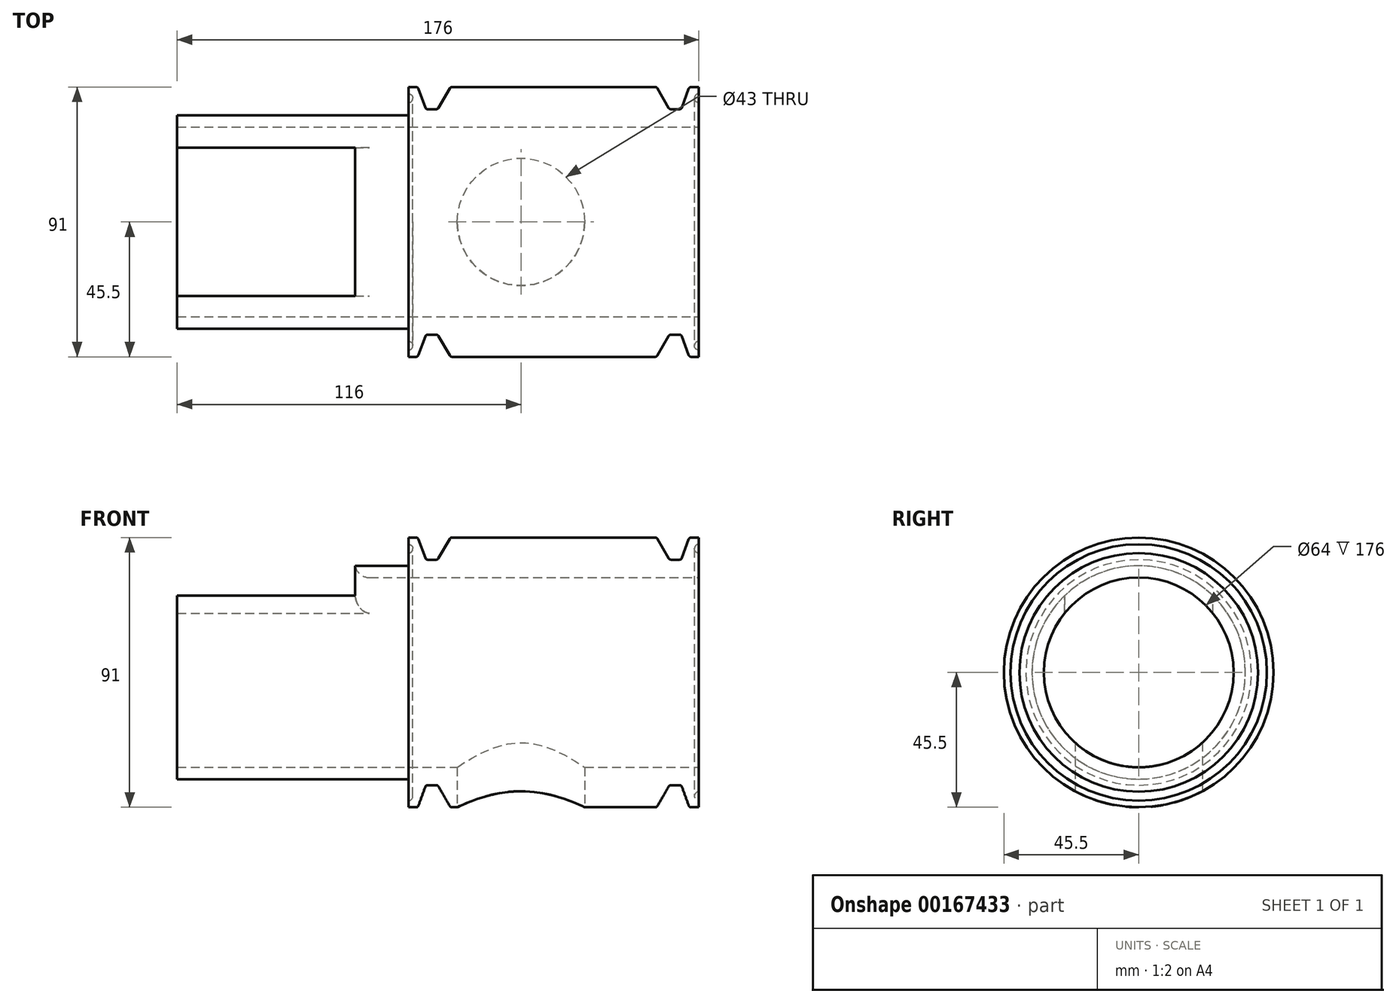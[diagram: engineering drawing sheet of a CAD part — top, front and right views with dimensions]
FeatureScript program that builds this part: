
annotation { "Feature Type Name" : "Feature", "Feature Type Description" : "" }
export const myFeature = defineFeature(function(context is Context, id is Id, definition is map)
    precondition{}
    {
        {
            var Q0;
            Q0=qCreatedBy(makeId("Front.planeOp"),FACE);
            var sketch = newSketch(context, id + "F0", { "sketchPlane" : qUnion([Q0])});
            skLineSegment(sketch, "E0", {"start": v(0, 0) * mm, "end": v(-76.74, 0) * mm, "construction": true});
            skLineSegment(sketch, "E1", {"start": v(-176, 32) * mm, "end": v(0, 32) * mm});
            skLineSegment(sketch, "E2", {"start": v(0, 32) * mm, "end": v(0, 40.25) * mm});
            skLineSegment(sketch, "E3", {"start": v(0, 45.5) * mm, "end": v(-2.64, 45.5) * mm});
            skLineSegment(sketch, "E4", {"start": v(-3.4, 44.97) * mm, "end": v(-5.72, 38.58) * mm});
            skLineSegment(sketch, "E5", {"start": v(-6.47, 38.05) * mm, "end": v(-9.45, 38.05) * mm});
            skLineSegment(sketch, "E6", {"start": v(-10.14, 38.45) * mm, "end": v(-13.98, 45.1) * mm});
            skLineSegment(sketch, "E7", {"start": v(-14.67, 45.5) * mm, "end": v(-83.33, 45.5) * mm});
            skLineSegment(sketch, "E8", {"start": v(-84.02, 45.1) * mm, "end": v(-87.86, 38.45) * mm});
            skLineSegment(sketch, "E9", {"start": v(-88.55, 38.05) * mm, "end": v(-91.53, 38.05) * mm});
            skLineSegment(sketch, "E10", {"start": v(-92.28, 38.58) * mm, "end": v(-94.6, 44.97) * mm});
            skLineSegment(sketch, "E11", {"start": v(-95.36, 45.5) * mm, "end": v(-98, 45.5) * mm});
            skLineSegment(sketch, "E12", {"start": v(-98, 45.5) * mm, "end": v(-98, 43.25) * mm});
            skLineSegment(sketch, "E13", {"start": v(-98, 36) * mm, "end": v(-176, 36) * mm});
            skLineSegment(sketch, "E14", {"start": v(-176, 36) * mm, "end": v(-176, 32) * mm});
            skArc(sketch, "E15", {"start": v(0, 43.25) * mm, "mid": v(-1.5, 41.75) * mm, "end": v(0, 40.25) * mm});
            skArc(sketch, "E16", {"start": v(-98, 40.25) * mm, "mid": v(-96.5, 41.75) * mm, "end": v(-98, 43.25) * mm});
            skLineSegment(sketch, "E17.trimOffspring", {"start": v(0, 43.25) * mm, "end": v(0, 45.5) * mm});
            skLineSegment(sketch, "E18.trimOffspring", {"start": v(-98, 40.25) * mm, "end": v(-98, 36) * mm});
            skPoint(sketch, "E19.visualSharp", {"position": v(-3.2, 45.5) * mm});
            skArc(sketch, "E19.filletArc", {"start": v(-2.64, 45.5) * mm, "mid": v(-3.1, 45.36) * mm, "end": v(-3.4, 44.97) * mm});
            skPoint(sketch, "E20.visualSharp", {"position": v(-5.91, 38.05) * mm});
            skArc(sketch, "E20.filletArc", {"start": v(-6.47, 38.05) * mm, "mid": v(-6.01, 38.2) * mm, "end": v(-5.72, 38.58) * mm});
            skPoint(sketch, "E21.visualSharp", {"position": v(-9.91, 38.05) * mm});
            skArc(sketch, "E21.filletArc", {"start": v(-10.14, 38.45) * mm, "mid": v(-9.85, 38.16) * mm, "end": v(-9.45, 38.05) * mm});
            skPoint(sketch, "E22.visualSharp", {"position": v(-14.21, 45.5) * mm});
            skArc(sketch, "E22.filletArc", {"start": v(-13.98, 45.1) * mm, "mid": v(-14.27, 45.4) * mm, "end": v(-14.67, 45.5) * mm});
            skPoint(sketch, "E23.visualSharp", {"position": v(-83.79, 45.5) * mm});
            skArc(sketch, "E23.filletArc", {"start": v(-83.33, 45.5) * mm, "mid": v(-83.73, 45.4) * mm, "end": v(-84.02, 45.1) * mm});
            skPoint(sketch, "E24.visualSharp", {"position": v(-88.09, 38.05) * mm});
            skArc(sketch, "E24.filletArc", {"start": v(-88.55, 38.05) * mm, "mid": v(-88.15, 38.16) * mm, "end": v(-87.86, 38.45) * mm});
            skPoint(sketch, "E25.visualSharp", {"position": v(-92.09, 38.05) * mm});
            skArc(sketch, "E25.filletArc", {"start": v(-92.28, 38.58) * mm, "mid": v(-91.99, 38.2) * mm, "end": v(-91.53, 38.05) * mm});
            skPoint(sketch, "E26.visualSharp", {"position": v(-94.8, 45.5) * mm});
            skArc(sketch, "E26.filletArc", {"start": v(-94.6, 44.97) * mm, "mid": v(-94.9, 45.36) * mm, "end": v(-95.36, 45.5) * mm});
            skSolve(sketch);
        }
        {
            var Q0;
            Q0 = qSketchRegion(id + "F0", true);
            var Q1;
            Q1=sQuery(id+"F0.wireOp",EDGE,"E0");
            revolve(context, id + "F1", {"entities" : qUnion([Q0]), "axis" : qUnion([Q1]), "revolveType" : RevolveType.FULL});
        }
        {
            var Q0;
            Q0=qCreatedBy(makeId("Top.planeOp"),FACE);
            cPlane(context, id + "F2", {"entities" : qUnion([Q0]), "cplaneType" : CPlaneType.OFFSET, "offset" : 45.5 * mm, "oppositeDirection" : true, "width" : 150 * mm, "height" : 150 * mm});
        }
        {
            var Q0;
            Q0=qCreatedBy(id+"F2.planeOp",FACE);
            var sketch = newSketch(context, id + "F3", { "sketchPlane" : qUnion([Q0])});
            skCircle(sketch, "E27", {"center": v(-60, 0) * mm, "radius": 21.5 * mm});
            skCircle(sketch, "E28", {"center": v(-60, 0) * mm, "radius": 25.4 * mm, "construction": true});
            skSolve(sketch);
        }
        {
            var Q0;
            Q0 = qSketchRegion(id + "F3", true);
            extrude(context, id + "F4", {"entities" : qUnion([Q0]), "operationType" : NewBodyOperationType.REMOVE, "depth" : 25 * mm});
        }
        {
            var Q0;
            Q0=qCreatedBy(makeId("Top.planeOp"),FACE);
            cPlane(context, id + "F5", {"entities" : qUnion([Q0]), "cplaneType" : CPlaneType.OFFSET, "offset" : 45.5 * mm, "width" : 150 * mm, "height" : 150 * mm});
        }
        {
            var Q0;
            Q0=qCreatedBy(id+"F5.planeOp",FACE);
            var sketch = newSketch(context, id + "F6", { "sketchPlane" : qUnion([Q0])});
            skLineSegment(sketch, "E29", {"start": v(0, 0) * mm, "end": v(-198.27, 0) * mm, "construction": true});
            skLineSegment(sketch, "E30.1", {"start": v(-176, 36) * mm, "end": v(-176, -36) * mm, "construction": true});
            skLineSegment(sketch, "E31.bottom", {"start": v(-176, 25) * mm, "end": v(-116, 25) * mm});
            skLineSegment(sketch, "E31.top", {"start": v(-176, -25) * mm, "end": v(-116, -25) * mm});
            skLineSegment(sketch, "E31.left", {"start": v(-176, 25) * mm, "end": v(-176, -25) * mm});
            skLineSegment(sketch, "E31.right", {"start": v(-116, 25) * mm, "end": v(-116, -25) * mm});
            skPoint(sketch, "E31.middle", {"position": v(-146, 0) * mm});
            skSolve(sketch);
        }
        {
            var Q0;
            Q0 = qSketchRegion(id + "F6", true);
            extrude(context, id + "F7", {"entities" : qUnion([Q0]), "operationType" : NewBodyOperationType.REMOVE, "oppositeDirection" : true, "depth" : 30 * mm});
        }
        {
            var Q0;
            Q0=makeQuery(id+"F7.boolean.opBoolean","INTERSECT",EDGE,{"derivedFrom":[makeQuery(id+"F1.opRevolve","SWEPT_FACE",FACE,{"disambiguationData":[OSD([sQuery(id+"F0.wireOp",EDGE,"E1")])]}),makeQuery(id+"F7.opExtrude","SWEPT_FACE",FACE,{"disambiguationData":[OSD([sQuery(id+"F6.wireOp",EDGE,"E31.right")])]})]});
            fillet(context, id + "F8", {"entities" : qUnion([Q0]), "radius" : 5 * mm, "tangentPropagation" : true, "allowEdgeOverflow" : false});
        }
    });
